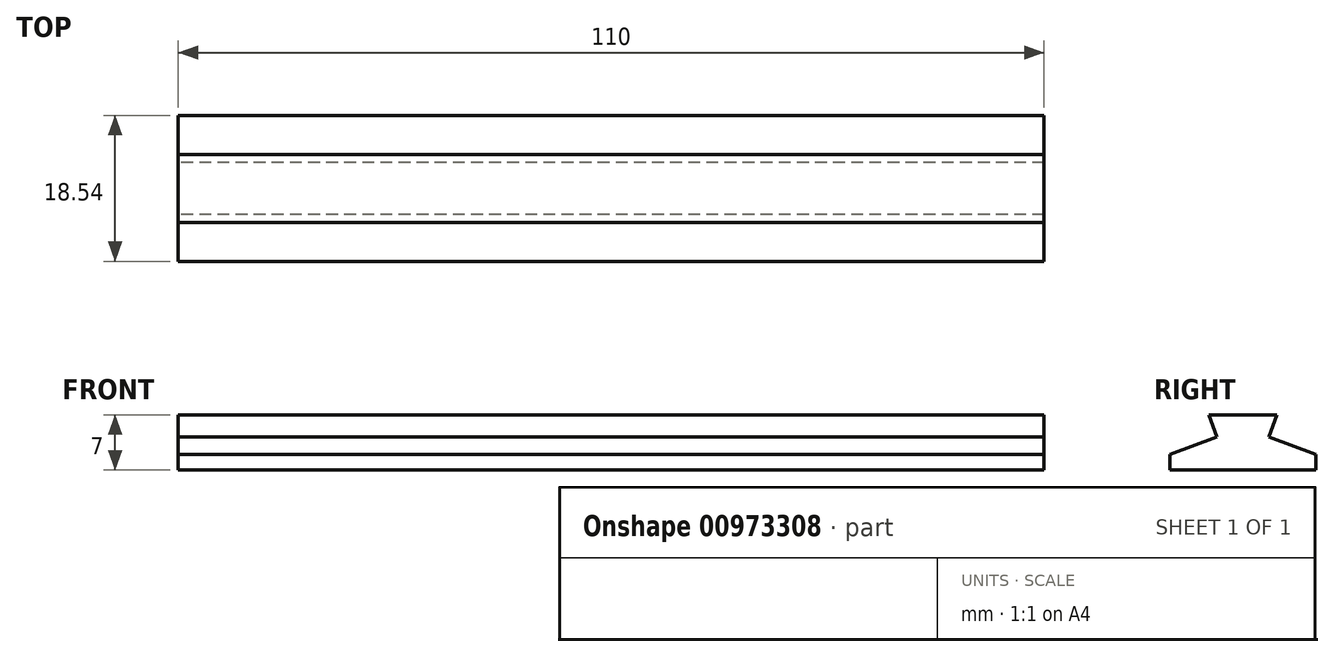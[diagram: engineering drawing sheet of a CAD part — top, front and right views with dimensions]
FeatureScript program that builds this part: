
annotation { "Feature Type Name" : "Feature", "Feature Type Description" : "" }
export const myFeature = defineFeature(function(context is Context, id is Id, definition is map)
    precondition{}
    {
        {
            assignVariable(context, id + "F0", {"name" : "railLength", "anyValue" : 110});
        }
        {
            var Q0;
            Q0=qCreatedBy(makeId("Right.planeOp"),FACE);
            var sketch = newSketch(context, id + "F1", { "sketchPlane" : qUnion([Q0])});
            skLineSegment(sketch, "E0.bottom", {"start": v(-2.5, 2.5) * mm, "end": v(2.5, 2.5) * mm});
            skLineSegment(sketch, "E0.top", {"start": v(-2.5, -2.5) * mm, "end": v(2.5, -2.5) * mm});
            skLineSegment(sketch, "E0.left", {"start": v(-2.5, 2.5) * mm, "end": v(-2.5, -2.5) * mm});
            skLineSegment(sketch, "E0.right", {"start": v(2.5, 2.5) * mm, "end": v(2.5, -2.5) * mm});
            skLineSegment(sketch, "E1", {"start": v(2.5, -2.5) * mm, "end": v(4.32, 2.5) * mm});
            skLineSegment(sketch, "E2", {"start": v(2.5, 2.5) * mm, "end": v(4.32, 2.5) * mm});
            skLineSegment(sketch, "E3", {"start": v(2.5, -2.5) * mm, "end": v(9.27, -2.5) * mm});
            skLineSegment(sketch, "E4", {"start": v(9.27, -2.5) * mm, "end": v(2.5, 0) * mm});
            skLineSegment(sketch, "E5.MirrorCS", {"start": v(-9.27, -2.5) * mm, "end": v(-2.5, 0) * mm});
            skLineSegment(sketch, "E6.MirrorCS", {"start": v(-2.5, -2.5) * mm, "end": v(-4.32, 2.5) * mm});
            skLineSegment(sketch, "E7.MirrorCS", {"start": v(-2.5, 2.5) * mm, "end": v(-4.32, 2.5) * mm});
            skLineSegment(sketch, "E8.MirrorCS", {"start": v(-2.5, -2.5) * mm, "end": v(-9.27, -2.5) * mm});
            skLineSegment(sketch, "E9.bottom", {"start": v(-9.27, -2.5) * mm, "end": v(9.27, -2.5) * mm});
            skLineSegment(sketch, "E9.top", {"start": v(-9.27, -4.5) * mm, "end": v(9.27, -4.5) * mm});
            skLineSegment(sketch, "E9.left", {"start": v(-9.27, -2.5) * mm, "end": v(-9.27, -4.5) * mm});
            skLineSegment(sketch, "E9.right", {"start": v(9.27, -2.5) * mm, "end": v(9.27, -4.5) * mm});
            skSolve(sketch);
        }
        {
            var Q0;
            {var subQ0=sQuery(id+"F1.wireOp",EDGE,"E3");var subQ2=sQuery(id+"F1.wireOp",EDGE,"E0.right");var subQ3=sQuery(id+"F1.wireOp",EDGE,"E0.top");var subQ5=sQuery(id+"F1.wireOp",EDGE,"E4");var subQ8=makeQuery(id+"F1.imprint","IMPRINT",EDGE,{"derivedFrom":subQ0});var subQ10=sQuery(id+"F1.wireOp",EDGE,"E8.MirrorCS");var subQ12=sQuery(id+"F1.wireOp",EDGE,"E0.left");var subQ14=sQuery(id+"F1.wireOp",EDGE,"E5.MirrorCS");var subQ15=makeQuery(id+"F1.imprint","INTERSECT",VERTEX,{"derivedFrom":[subQ12,subQ14]});var subQ18=makeQuery(id+"F1.imprint","IMPRINT",EDGE,{"disambiguationData":[TD([[subQ15,1.0]])],"derivedFrom":subQ14});var subQ20=sQuery(id+"F1.wireOp",EDGE,"E2");var subQ21=sQuery(id+"F1.wireOp",EDGE,"E0.bottom");var subQ22=makeQuery(id+"F1.imprint","INTERSECT",VERTEX,{"derivedFrom":[subQ2,subQ5]});var subQ24=makeQuery(id+"F1.imprint","IMPRINT",EDGE,{"disambiguationData":[TD([[subQ22,1.0]])],"derivedFrom":subQ5});var subQ25=sQuery(id+"F1.wireOp",EDGE,"E7.MirrorCS");var subQ27=makeQuery(id+"F1.imprint","IMPRINT",EDGE,{"derivedFrom":subQ3});var subQ29=makeQuery(id+"F1.imprint","IMPRINT",EDGE,{"derivedFrom":subQ10});Q0=qUnion([makeQuery(id+"F1.imprint","IMPRINT",FACE,{"disambiguationData":[TD([[subQ29,-1.0]])]}),makeQuery(id+"F1.imprint","IMPRINT",FACE,{"disambiguationData":[TD([[subQ24,1.0]])]}),makeQuery(id+"F1.imprint","IMPRINT",FACE,{"disambiguationData":[TD([[makeQuery(id+"F1.imprint","IMPRINT",EDGE,{"derivedFrom":subQ25}),1.0]])]}),makeQuery(id+"F1.imprint","IMPRINT",FACE,{"disambiguationData":[TD([[subQ27,-1.0]])]}),makeQuery(id+"F1.imprint","IMPRINT",FACE,{"disambiguationData":[TD([[makeQuery(id+"F1.imprint","IMPRINT",EDGE,{"derivedFrom":subQ21}),-1.0]])]}),makeQuery(id+"F1.imprint","IMPRINT",FACE,{"disambiguationData":[TD([[makeQuery(id+"F1.imprint","IMPRINT",EDGE,{"derivedFrom":subQ20}),-1.0]])]}),makeQuery(id+"F1.imprint","IMPRINT",FACE,{"disambiguationData":[TD([[subQ18,-1.0]])]}),makeQuery(id+"F1.imprint","IMPRINT",FACE,{"disambiguationData":[TD([[subQ8,1.0]])]})]);}
            extrude(context, id + "F2", {"entities" : qUnion([Q0]), "depth" : (getVariable(context, 'railLength') / 2) * mm, "offsetDistance" : 25 * mm, "hasSecondDirection" : true, "secondDirectionOppositeDirection" : true, "secondDirectionDepth" : (getVariable(context, 'railLength') / 2) * mm});
        }
    });
